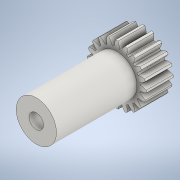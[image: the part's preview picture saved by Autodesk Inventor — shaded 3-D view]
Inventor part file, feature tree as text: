
AUTODESK INVENTOR PART (.ipt)
format: ipt  version: 2022.1 (Build 261234000, 234)  size: 239,616 bytes
history: native  units: mm (DEFAULTED — no unit token found)
features: sketch x4, extrude x3, plane x3, other x3
ambient origin geometry x8: Origin, YZ Plane, XZ Plane, XY Plane, X Axis, Y Axis, Z Axis, Center Point
bodies: Solid1 (feature_tree)
feature tree (13):
  extrude  "Extrusion1"  Depth=12.7mm TaperAngle=0.0deg
  plane  "Work Plane1"
  plane  "Work Plane2"
  plane  "Work Plane3"
  other  "Spur Gear"
  extrude  "Extrusion2"  Depth=76.2mm TaperAngle=0.0deg
  extrude  "Extrusion3"  TaperAngle=0.0deg  [1 undecoded]
  sketch  "Sketch1"  dims[d0=27.94mm d1=12.7mm d2=0.0mm]
  sketch  "Sketch2"  dims[d3=25.4mm d4=76.2mm d5=0.0mm]
  other  "Srf1"
  sketch  "Sketch3"  dims[d6=0.0mm d7=1.570796mm d9=0.0mm]
  sketch  "Sketch4"  dims[d14=0.0mm d15=71.755mm d16=0.0mm d17=0.0mm d18=0.0mm d19=71.755mm d20=19.05mm d21=38.1mm d22=0.0mm d23=6.858mm d24=0.0mm d25=0.0mm]
  other  "Pitch Diameter"
note: 1 required parameter value undecoded (feature->parameter linkage not recoverable at this tier; creation-order binding heuristic only, values carry confidence <= 0.55)
